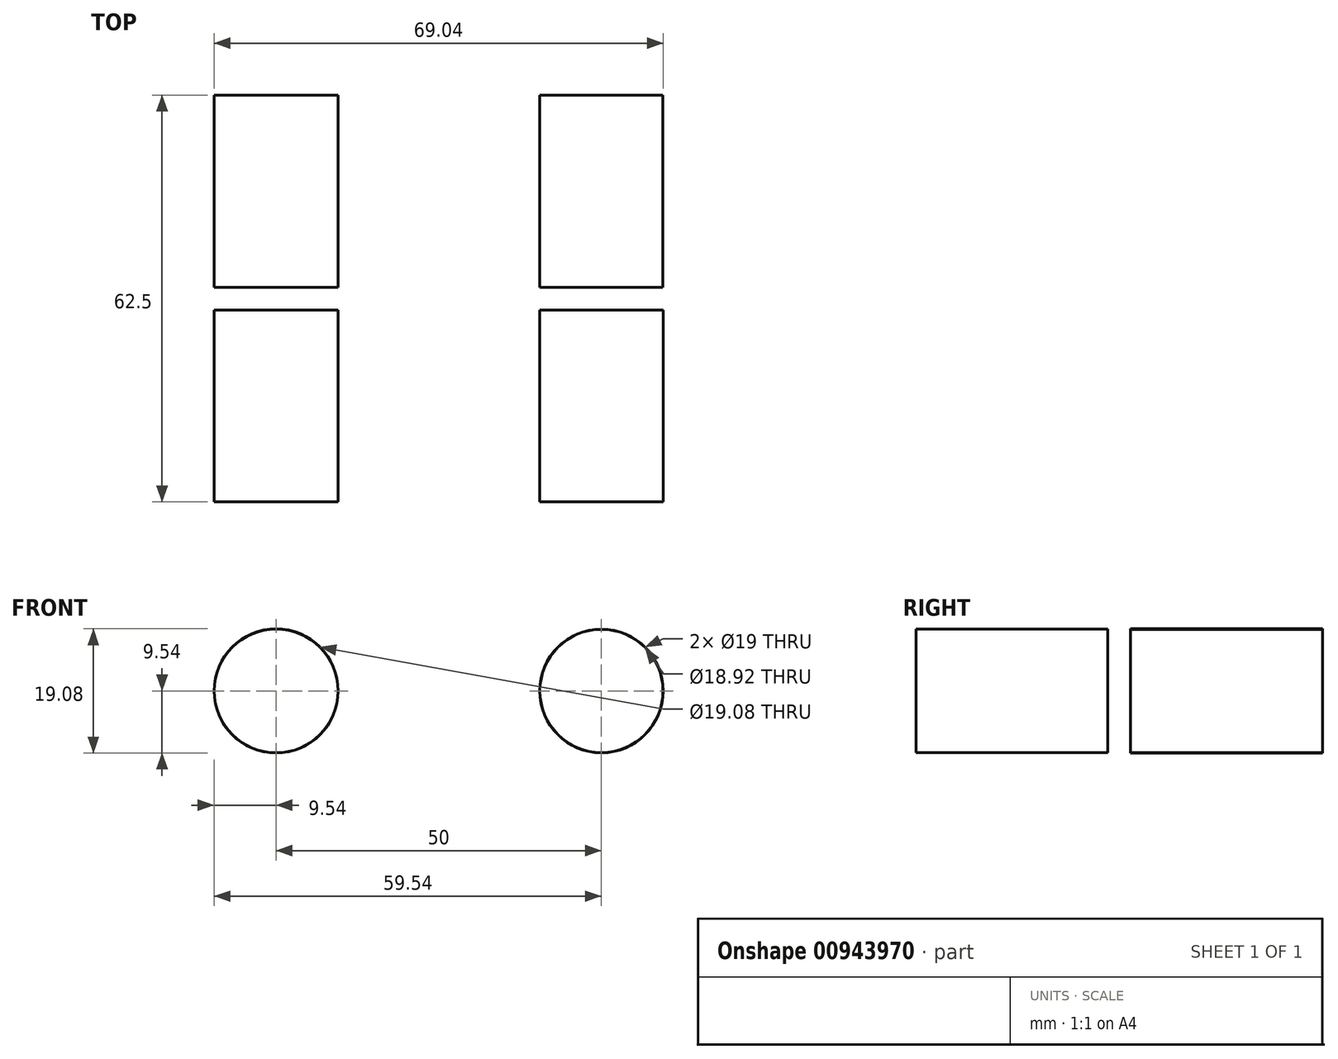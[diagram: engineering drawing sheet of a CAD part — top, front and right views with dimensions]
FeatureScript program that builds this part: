
annotation { "Feature Type Name" : "Feature", "Feature Type Description" : "" }
export const myFeature = defineFeature(function(context is Context, id is Id, definition is map)
    precondition{}
    {
        {
            var Q0;
            Q0=qCreatedBy(makeId("Front.planeOp"),FACE);
            var sketch = newSketch(context, id + "F0", { "sketchPlane" : qUnion([Q0])});
            skLineSegment(sketch, "E0", {"start": v(-25, 0) * mm, "end": v(25, 0) * mm});
            skCircle(sketch, "E1", {"center": v(25, 0) * mm, "radius": 9.5 * mm});
            skCircle(sketch, "E2", {"center": v(-25, 0) * mm, "radius": 9.5 * mm});
            skSolve(sketch);
        }
        {
            var Q0;
            Q0=qCreatedBy(makeId("Front.planeOp"),FACE);
            cPlane(context, id + "F1", {"entities" : qUnion([Q0]), "cplaneType" : CPlaneType.OFFSET, "offset" : 30 * mm, "oppositeDirection" : true, "width" : 150 * mm, "height" : 150 * mm});
        }
        {
            var Q0;
            Q0=sQuery(id+"F0.wireOp",EDGE,"E1");
            var Q1;
            Q1=sQuery(id+"F0.wireOp",EDGE,"E2");
            extrude(context, id + "F2", {"bodyType" : ToolBodyType.SURFACE, "surfaceEntities" : qUnion([Q0, Q1]), "oppositeDirection" : true, "depth" : 29.5 * mm, "offsetDistance" : 25 * mm});
        }
        {
            var Q0;
            Q0=qCreatedBy(id+"F1.planeOp",FACE);
            cPlane(context, id + "F3", {"entities" : qUnion([Q0]), "cplaneType" : CPlaneType.OFFSET, "offset" : 3 * mm, "oppositeDirection" : true, "width" : 150 * mm, "height" : 150 * mm});
        }
        {
            var Q0;
            Q0=qCreatedBy(id+"F3.planeOp",FACE);
            var sketch = newSketch(context, id + "F4", { "sketchPlane" : qUnion([Q0])});
            skCircle(sketch, "E3.0", {"center": v(25, 0) * mm, "radius": 9.5 * mm});
            skCircle(sketch, "E4.0", {"center": v(-25, 0) * mm, "radius": 9.5 * mm});
            skCircle(sketch, "E5", {"center": v(25, 0) * mm, "radius": 9.46 * mm});
            skCircle(sketch, "E6", {"center": v(-25, 0) * mm, "radius": 9.54 * mm});
            skSolve(sketch);
        }
        {
            var Q0;
            Q0=sQuery(id+"F4.wireOp",EDGE,"E6");
            var Q1;
            Q1=sQuery(id+"F4.wireOp",EDGE,"E5");
            extrude(context, id + "F5", {"bodyType" : ToolBodyType.SURFACE, "surfaceEntities" : qUnion([Q0, Q1]), "oppositeDirection" : true, "depth" : 29.5 * mm, "offsetDistance" : 25 * mm});
        }
    });
